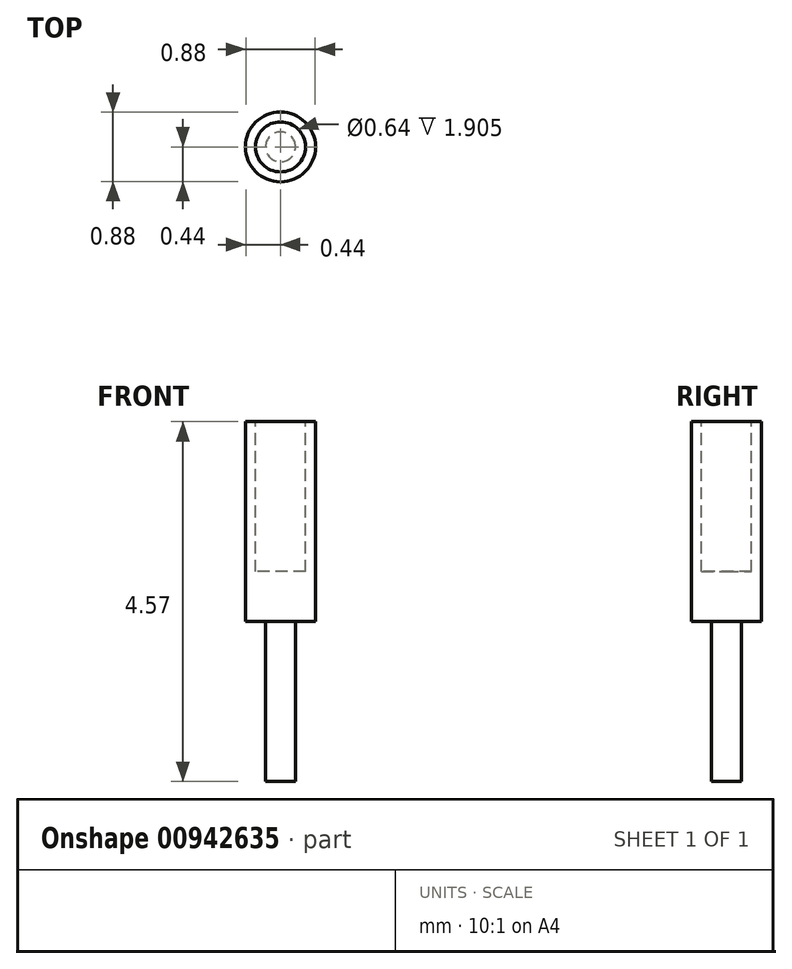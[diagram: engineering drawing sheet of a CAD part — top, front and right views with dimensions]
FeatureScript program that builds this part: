
annotation { "Feature Type Name" : "Feature", "Feature Type Description" : "" }
export const myFeature = defineFeature(function(context is Context, id is Id, definition is map)
    precondition{}
    {
        {
            var Q0;
            Q0=qCreatedBy(makeId("Top.planeOp"),FACE);
            var sketch = newSketch(context, id + "F0", { "sketchPlane" : qUnion([Q0])});
            skCircle(sketch, "E0", {"center": v(0, 0) * mm, "radius": 0.44 * mm});
            skCircle(sketch, "E1", {"center": v(0, 0) * mm, "radius": 0.32 * mm});
            skSolve(sketch);
        }
        {
            var Q0;
            Q0=makeQuery(id+"F0.imprint","IMPRINT",FACE,{"disambiguationData":[TD([[makeQuery(id+"F0.imprint","IMPRINT",EDGE,{"derivedFrom":sQuery(id+"F0.wireOp",EDGE,"E0")}),1.0]])]});
            extrude(context, id + "F1", {"entities" : qUnion([Q0]), "oppositeDirection" : true, "depth" : 1.9 * mm, "offsetDistance" : 25.4 * mm});
        }
        {
            var Q0;
            Q0=makeQuery(id+"F1.opExtrude","CAP_FACE",FACE,{"disambiguationData":[OSD([sQuery(id+"F0.wireOp",EDGE,"E0"),sQuery(id+"F0.wireOp",EDGE,"E1")])],"isStart":false});
            var sketch = newSketch(context, id + "F2", { "sketchPlane" : qUnion([Q0])});
            skCircle(sketch, "E2.0", {"center": v(0, 0) * mm, "radius": 0.44 * mm});
            skSolve(sketch);
        }
        {
            var Q0;
            Q0 = qSketchRegion(id + "F2", true);
            extrude(context, id + "F3", {"entities" : qUnion([Q0]), "operationType" : NewBodyOperationType.ADD, "depth" : 0.64 * mm, "offsetDistance" : 25.4 * mm});
        }
        {
            var Q0;
            Q0=makeQuery(id+"F3.opExtrude","CAP_FACE",FACE,{"disambiguationData":[OSD([sQuery(id+"F2.wireOp",EDGE,"E2.0")])],"isStart":false});
            var sketch = newSketch(context, id + "F4", { "sketchPlane" : qUnion([Q0])});
            skCircle(sketch, "E3.0", {"center": v(0, 0) * mm, "radius": 0.2 * mm});
            skSolve(sketch);
        }
        {
            var Q0;
            Q0 = qSketchRegion(id + "F4", true);
            extrude(context, id + "F5", {"entities" : qUnion([Q0]), "operationType" : NewBodyOperationType.ADD, "depth" : 2.03 * mm, "offsetDistance" : 25.4 * mm});
        }
    });
